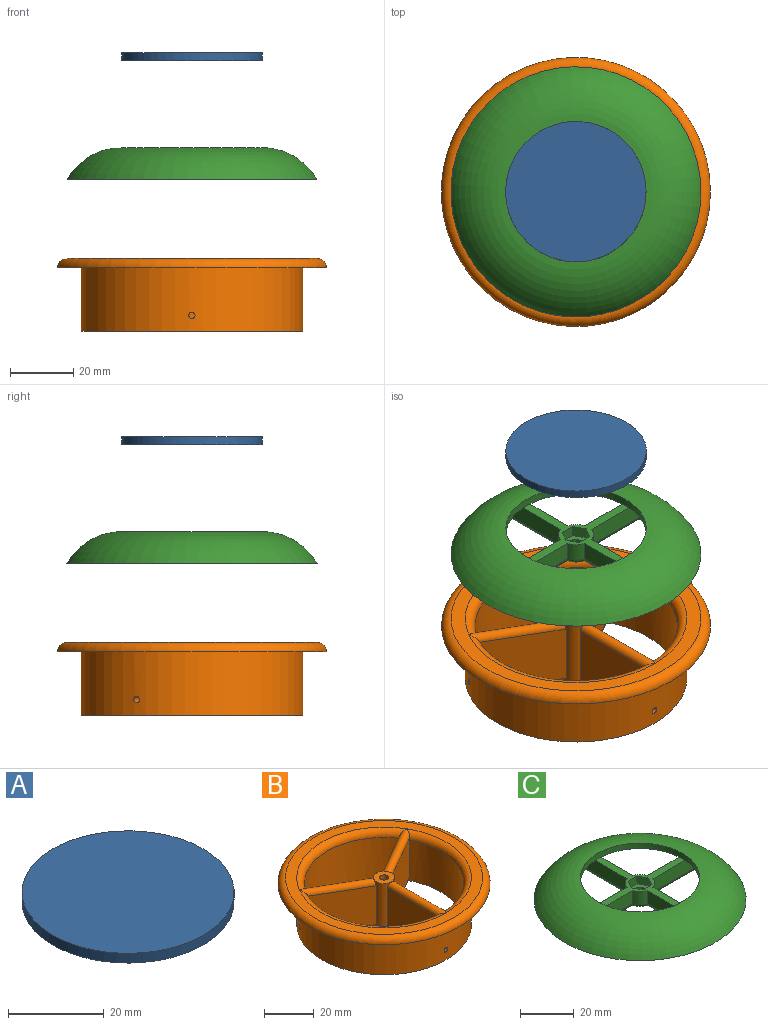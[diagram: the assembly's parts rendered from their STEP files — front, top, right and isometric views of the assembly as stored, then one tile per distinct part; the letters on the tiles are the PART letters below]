
ASSEMBLY  parts=3 mates=4
PART A: 3 faces, bbox 44.4x44.4x2.5 mm
  f0: cylinder r=22.18mm len=44.36mm, axis (0,0,-1), area 348.4mm2, adj f1,f2
  f1: plane 44.36x44.36mm, normal (0,0,1), area 1545.4mm2, adj f0
  f2: plane 44.36x44.36mm, normal (0,0,-1), area 1545.4mm2, adj f0
PART B: 35 faces, bbox 92x92x23 mm
  f0: cylinder r=1mm len=9.66mm, axis (0.87,0.5,0), area 62.8mm2, adj f1,f6
  f1: plane 2x1.73mm, normal (0.87,0.5,0), area 3.1mm2, adj f0
  f2: cylinder r=1mm len=9.66mm, axis (-0.87,0.5,0), area 62.8mm2, adj f3,f6
  f3: plane 2x1.73mm, normal (-0.87,0.5,0), area 3.1mm2, adj f2
  f4: plane 70x70mm, normal (0,0,-1), area 631.5mm2, adj f6,f13,f16,f19
  f5: plane 79x79mm, normal (0,0,1), area 1053.2mm2, adj f23,f30,f31,f32
  f6: cylinder r=35mm len=70mm, axis (0,0,1), area 4388.8mm2, adj f0,f2,f4,f22,f33
  f7: plane 28.31x19.01mm, normal (1,0,0), area 534.5mm2, adj f8,f19,f25,f28,f30
  f8: cylinder r=4.3mm len=23mm, axis (0,0,1), area 115.2mm2, adj f7,f9,f20,f21,f24,f25,f27,f28
  f9: plane 24.52x19.01mm, normal (0.5,-0.87,0), area 534.5mm2, adj f8,f19,f24,f27,f30
  f10: plane 24.52x19.01mm, normal (-0.5,0.87,0), area 534.5mm2, adj f11,f16,f24,f27,f32
  f11: cylinder r=4.3mm len=23mm, axis (0,0,1), area 115.2mm2, adj f10,f12,f20,f21,f24,f26,f27,f29
  f12: plane 24.52x19.01mm, normal (0.5,0.87,0), area 534.5mm2, adj f11,f16,f26,f29,f32
  f13: cylinder r=32mm len=48mm, axis (0,0,1), area 1262.1mm2, adj f4,f14,f18,f28,f29,f31
  f14: plane 24.52x19.01mm, normal (-0.5,-0.87,0), area 534.5mm2, adj f13,f15,f26,f29,f31
  f15: cylinder r=4.3mm len=23mm, axis (0,0,1), area 115.2mm2, adj f14,f18,f20,f21,f25,f26,f28,f29
  f16: cylinder r=32mm len=55.43mm, axis (0,0,1), area 1262.1mm2, adj f4,f10,f12,f27,f29,f32
  f17: cylinder r=1.8mm len=23mm, axis (0,0,1), area 260.1mm2, adj f20,f21
  f18: plane 28.31x19.01mm, normal (-1,0,0), area 534.5mm2, adj f13,f15,f25,f28,f31
  f19: cylinder r=32mm len=48mm, axis (0,0,1), area 1262.1mm2, adj f4,f7,f9,f27,f28,f30
  f20: plane 8.6x8.6mm, normal (0,0,-1), area 47.9mm2, adj f8,f11,f15,f17
  f21: plane 8.6x8.6mm, normal (0,0,1), area 47.9mm2, adj f8,f11,f15,f17
  f22: plane 85x85mm, normal (0,0,-1), area 1826.1mm2, adj f6,f23
  f23: torus R=39.5mm, axis (0,0,1), area 1226.1mm2, adj f5,f22
  f24: cylinder r=2mm len=29.01mm, axis (-0.87,-0.5,0), area 183.9mm2, adj f8,f9,f10,f11,f30,f32
  f25: cylinder r=2mm len=31.19mm, axis (0,-1,0), area 183.9mm2, adj f7,f8,f15,f18,f30,f31
  f26: cylinder r=2mm len=29.01mm, axis (0.87,-0.5,0), area 183.9mm2, adj f11,f12,f14,f15,f31,f32
  f27: cylinder r=2mm len=26.42mm, axis (0.87,0.5,0), area 175.4mm2, adj f8,f9,f10,f11,f16,f19
  f28: cylinder r=2mm len=28.19mm, axis (0,1,0), area 175.4mm2, adj f7,f8,f13,f15,f18,f19
  f29: cylinder r=2mm len=26.42mm, axis (-0.87,0.5,0), area 175.4mm2, adj f11,f12,f13,f14,f15,f16
  f30: torus R=35mm, axis (0,0,1), area 313.3mm2, adj f5,f7,f9,f19,f24,f25
  f31: torus R=35mm, axis (0,0,1), area 313.3mm2, adj f5,f13,f14,f18,f25,f26
  f32: torus R=35mm, axis (0,0,1), area 313.3mm2, adj f5,f10,f12,f16,f24,f26
  f33: cylinder r=1mm len=10mm, axis (0,-1,0), area 62.8mm2, adj f6,f34
  f34: plane 2x2mm, normal (0,-1,0), area 3.1mm2, adj f33
PART C: 41 faces, bbox 92x92x20 mm
  f0: plane 79x79mm, normal (0,0,-1), area 135.6mm2, adj f5,f37,f38,f39,f40
  f1: torus R=22.18mm, axis (0,0,-1), area 629mm2, adj f8,f18,f20,f37
  f2: torus R=22.18mm, axis (0,0,-1), area 629mm2, adj f9,f11,f20,f38
  f3: torus R=22.18mm, axis (0,0,-1), area 629mm2, adj f15,f17,f20,f39
  f4: plane 8x8mm, normal (0,0,-1), area 34.4mm2, adj f28,f30,f32,f34,f36
  f5: torus R=22.18mm, axis (0,0,-1), area 4175.3mm2, adj f0,f20
  f6: torus R=22.18mm, axis (0,0,-1), area 629mm2, adj f12,f14,f20,f40
  f7: cylinder r=5.5mm len=6mm, axis (0,0,-1), area 33.6mm2, adj f8,f18,f19,f34
  f8: plane 30.06x6mm, normal (0,1,0), area 156mm2, adj f1,f7,f19,f31,f37
  f9: plane 30.06x6mm, normal (0,-1,0), area 156mm2, adj f2,f10,f19,f31,f38
  f10: cylinder r=5.5mm len=6mm, axis (0,0,-1), area 33.6mm2, adj f9,f11,f19,f30
  f11: plane 30.06x6mm, normal (-1,0,0), area 156mm2, adj f2,f10,f19,f29,f38
  f12: plane 30.06x6mm, normal (1,0,0), area 156mm2, adj f6,f13,f19,f29,f40
  f13: cylinder r=5.5mm len=6mm, axis (0,0,-1), area 33.6mm2, adj f12,f14,f19,f32
  f14: plane 30.06x6mm, normal (0,-1,0), area 156mm2, adj f6,f13,f19,f33,f40
  f15: plane 30.06x6mm, normal (0,1,0), area 156mm2, adj f3,f16,f19,f33,f39
  f16: cylinder r=5.5mm len=6mm, axis (0,0,-1), area 33.6mm2, adj f15,f17,f19,f36
  f17: plane 30.06x6mm, normal (1,0,0), area 156mm2, adj f3,f16,f19,f35,f39
  f18: plane 30.06x6mm, normal (-1,0,0), area 156mm2, adj f1,f7,f19,f35,f37
  f19: plane 44.36x44.36mm, normal (0,0,1), area 243.1mm2, adj f7,f8,f9,f10,f11,f12,f13,f14
  f20: cylinder r=22.18mm len=44.36mm, axis (0,0,1), area 348.4mm2, adj f1,f2,f3,f5,f6,f19
  f21: plane 3.9x3.5mm, normal (-0.87,0.5,0), area 15.8mm2, adj f19,f22,f26,f27
  f22: plane 3.9x3.5mm, normal (-0.87,-0.5,0), area 15.8mm2, adj f19,f21,f23,f27
  f23: plane 4.5x3.5mm, normal (0,-1,0), area 15.8mm2, adj f19,f22,f24,f27
  f24: plane 3.9x3.5mm, normal (0.87,-0.5,0), area 15.8mm2, adj f19,f23,f25,f27
  f25: plane 3.9x3.5mm, normal (0.87,0.5,0), area 15.8mm2, adj f19,f24,f26,f27
  f26: plane 4.5x3.5mm, normal (0,1,0), area 15.8mm2, adj f19,f21,f25,f27
  f27: plane 9.01x7.8mm, normal (0,0,1), area 36.8mm2, adj f21,f22,f23,f24,f25,f26,f28
  f28: cylinder r=2.25mm len=4.5mm, axis (0,0,1), area 56.5mm2, adj f4,f27
  f29: cylinder r=1.5mm len=34.95mm, axis (0,-1,0), area 151.4mm2, adj f11,f12,f30,f32,f38,f40
  f30: torus R=4mm, axis (0,0,1), area 13.8mm2, adj f4,f10,f29,f31
  f31: cylinder r=1.5mm len=34.95mm, axis (1,0,0), area 151.4mm2, adj f8,f9,f30,f34,f37,f38
  f32: torus R=4mm, axis (0,0,1), area 13.8mm2, adj f4,f13,f29,f33
  f33: cylinder r=1.5mm len=34.95mm, axis (1,0,0), area 151.4mm2, adj f14,f15,f32,f36,f39,f40
  f34: torus R=4mm, axis (0,0,1), area 13.8mm2, adj f4,f7,f31,f35
  f35: cylinder r=1.5mm len=34.95mm, axis (0,-1,0), area 151.4mm2, adj f17,f18,f34,f36,f37,f39
  f36: torus R=4mm, axis (0,0,1), area 13.8mm2, adj f4,f16,f33,f35
  f37: torus R=38.95mm, axis (0,0,1), area 236.2mm2, adj f0,f1,f8,f18,f31,f35
  f38: torus R=38.95mm, axis (0,0,1), area 236.2mm2, adj f0,f2,f9,f11,f29,f31
  f39: torus R=38.95mm, axis (0,0,1), area 236.2mm2, adj f0,f3,f15,f17,f33,f35
  f40: torus R=38.95mm, axis (0,0,1), area 236.2mm2, adj f0,f6,f12,f14,f29,f33
PLACE A rot(axis=(0,0,1),43.6deg) t=(0,0,62.5)mm
PLACE B t=(0,0,-3)mm
PLACE C t=(0,0,25)mm
MATE planar C.f10 <-> B.f8  axis (0,0,-1) through (0,0,25)mm
MATE cylindrical A.f0 <-> C.f10  axis (0,0,-1) through (0,0,62.5)mm
MATE cylindrical C.f28 <-> B.f17  axis (0,0,1) through (0,0,25)mm
MATE planar A.f0 <-> C.f1  axis (0,0,-1) through (0,0,62.5)mm
